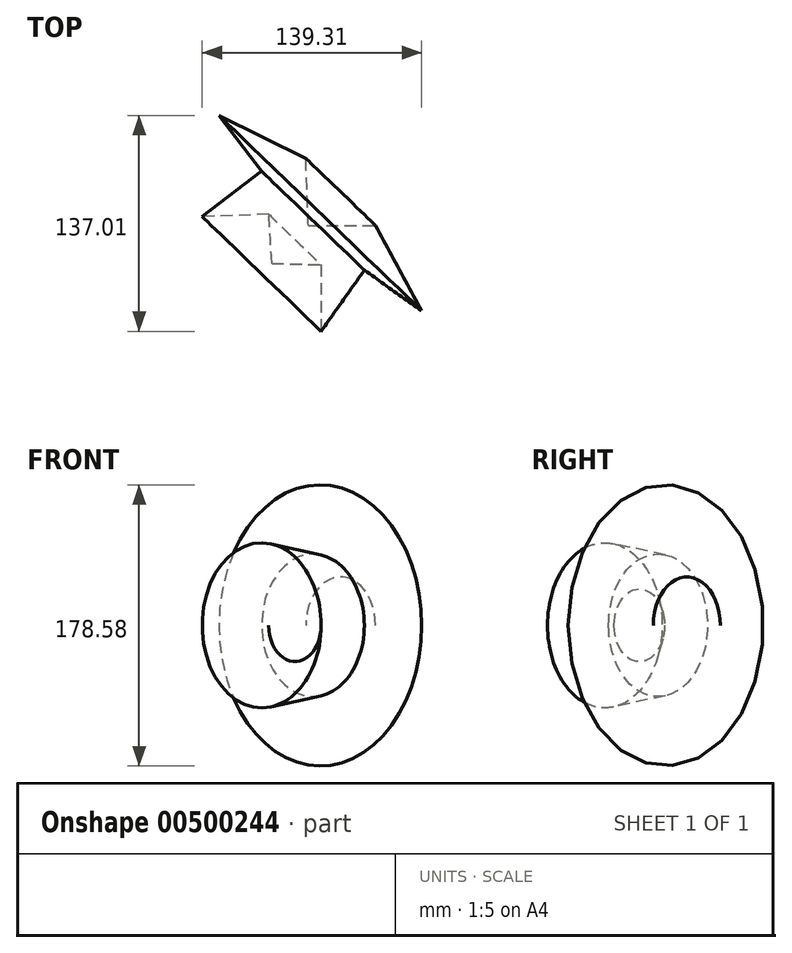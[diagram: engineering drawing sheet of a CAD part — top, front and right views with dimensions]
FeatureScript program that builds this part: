
annotation { "Feature Type Name" : "Feature", "Feature Type Description" : "" }
export const myFeature = defineFeature(function(context is Context, id is Id, definition is map)
    precondition{}
    {
        {
            var Q0;
            Q0=qCreatedBy(makeId("Top.planeOp"),FACE);
            var sketch = newSketch(context, id + "F0", { "sketchPlane" : qUnion([Q0])});
            skLineSegment(sketch, "E0", {"start": v(-58.67, 23.09) * mm, "end": v(-35.57, 47.06) * mm});
            skLineSegment(sketch, "E1", {"start": v(-35.57, 47.06) * mm, "end": v(7.15, 47.06) * mm});
            skLineSegment(sketch, "E2", {"start": v(7.15, 47.06) * mm, "end": v(36.35, -6.99) * mm});
            skLineSegment(sketch, "E3", {"start": v(36.35, -6.99) * mm, "end": v(0, 18.73) * mm});
            skLineSegment(sketch, "E4", {"start": v(0, 18.73) * mm, "end": v(-27.45, -20.08) * mm});
            skLineSegment(sketch, "E5", {"start": v(-27.45, -20.08) * mm, "end": v(-27.45, 22.22) * mm});
            skLineSegment(sketch, "E6", {"start": v(-27.45, 22.22) * mm, "end": v(-58.67, 23.09) * mm});
            skSolve(sketch);
        }
        {
            var Q0;
            Q0=makeQuery(id+"F0.imprint","IMPRINT",FACE,{"disambiguationData":[TD([[makeQuery(id+"F0.imprint","IMPRINT",EDGE,{"derivedFrom":sQuery(id+"F0.wireOp",EDGE,"E0")}),-1.0]])]});
            var Q1;
            Q1=sQuery(id+"F0.wireOp",EDGE,"E0");
            revolve(context, id + "F1", {"entities" : qUnion([Q0]), "axis" : qUnion([Q1]), "revolveType" : RevolveType.FULL});
        }
    });
